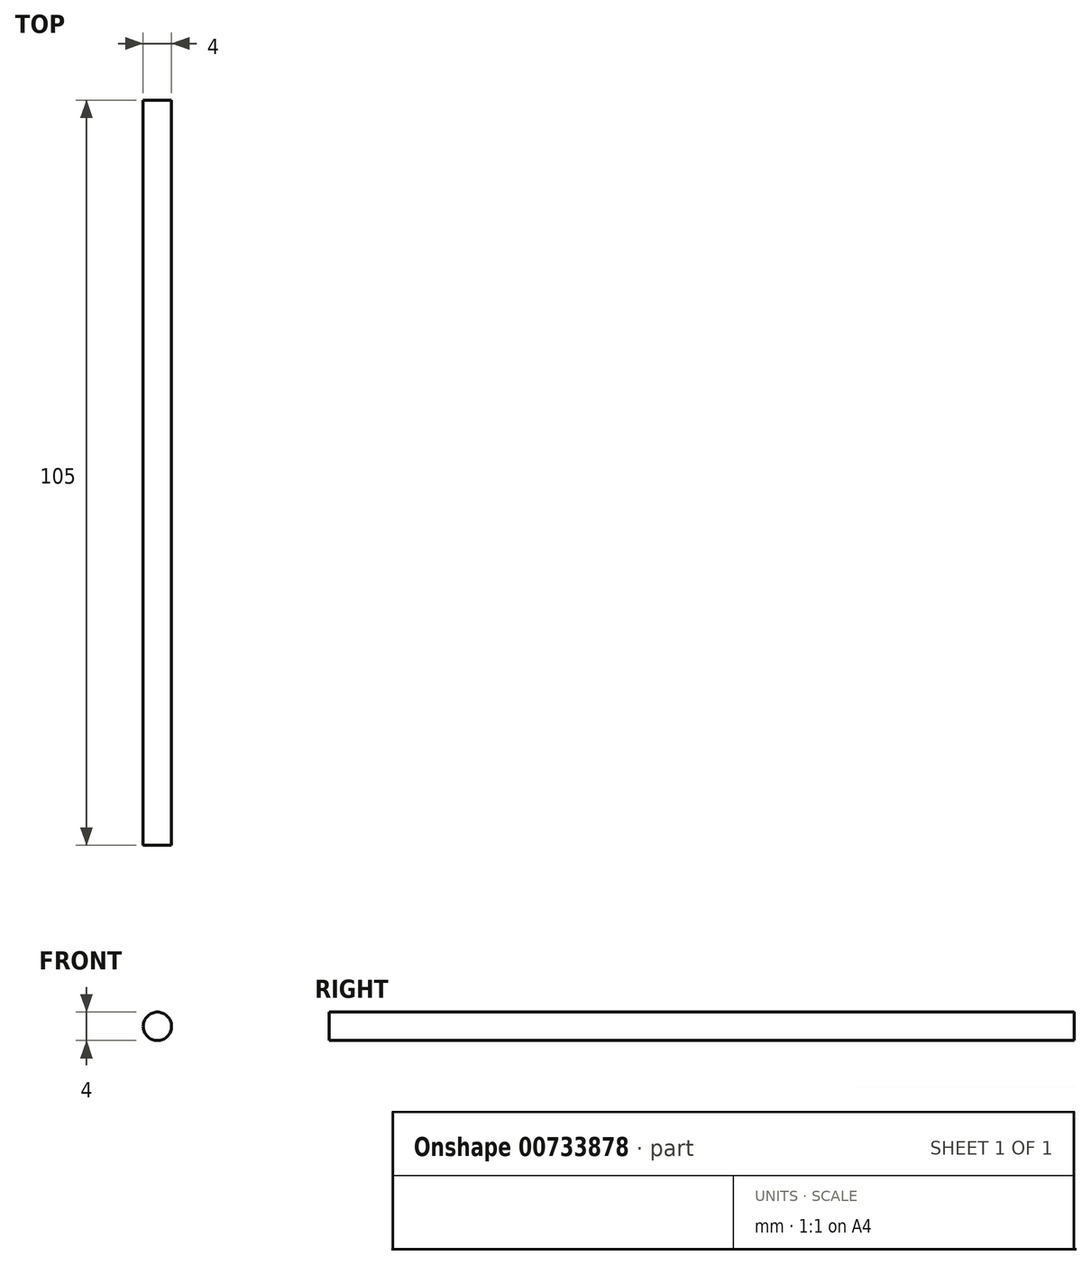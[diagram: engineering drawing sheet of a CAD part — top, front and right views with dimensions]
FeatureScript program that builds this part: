
annotation { "Feature Type Name" : "Feature", "Feature Type Description" : "" }
export const myFeature = defineFeature(function(context is Context, id is Id, definition is map)
    precondition{}
    {
        {
            var Q0;
            Q0=qCreatedBy(makeId("Front.planeOp"),FACE);
            var sketch = newSketch(context, id + "F0", { "sketchPlane" : qUnion([Q0])});
            skCircle(sketch, "E0", {"center": v(0, 0) * mm, "radius": 2 * mm});
            skSolve(sketch);
        }
        {
            var Q0;
            Q0=makeQuery(id+"F0.imprint","IMPRINT",FACE,{"disambiguationData":[TD([[makeQuery(id+"F0.imprint","IMPRINT",EDGE,{"derivedFrom":sQuery(id+"F0.wireOp",EDGE,"E0")}),1.0]])]});
            extrude(context, id + "F1", {"entities" : qUnion([Q0]), "depth" : (145 - 40) * mm, "offsetDistance" : 25 * mm});
        }
    });
